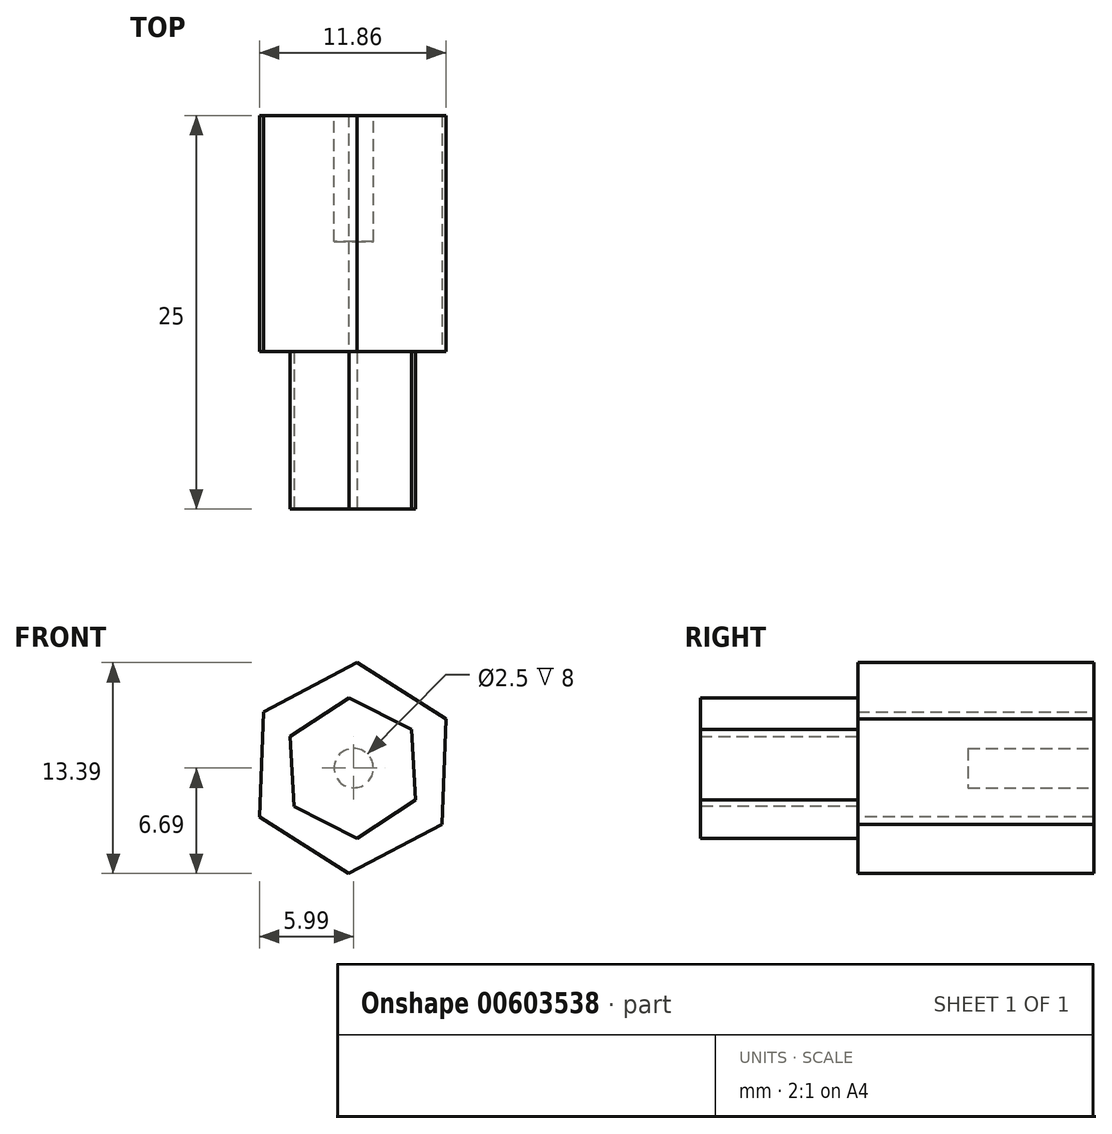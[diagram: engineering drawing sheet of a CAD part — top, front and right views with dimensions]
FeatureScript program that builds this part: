
annotation { "Feature Type Name" : "Feature", "Feature Type Description" : "" }
export const myFeature = defineFeature(function(context is Context, id is Id, definition is map)
    precondition{}
    {
        {
            var Q0;
            Q0=qCreatedBy(makeId("Front.planeOp"),FACE);
            var sketch = newSketch(context, id + "F0", { "sketchPlane" : qUnion([Q0])});
            skCircle(sketch, "E0", {"center": v(0, 0) * mm, "radius": 6.75 * mm, "construction": true});
            skCircle(sketch, "E1", {"center": v(0, 0) * mm, "radius": 4.5 * mm, "construction": true});
            skLineSegment(sketch, "E2", {"start": v(-5.99, -3.12) * mm, "end": v(-5.72, 3.58) * mm});
            skLineSegment(sketch, "E3.1.0", {"start": v(-0.32, -6.7) * mm, "end": v(-5.99, -3.12) * mm});
            skLineSegment(sketch, "E3.2.0", {"start": v(5.6, -3.57) * mm, "end": v(-0.32, -6.7) * mm});
            skLineSegment(sketch, "E3.3.0", {"start": v(5.87, 3.12) * mm, "end": v(5.6, -3.57) * mm});
            skLineSegment(sketch, "E3.4.0", {"start": v(0.2, 6.7) * mm, "end": v(5.87, 3.12) * mm});
            skLineSegment(sketch, "E3.5.0", {"start": v(-5.72, 3.58) * mm, "end": v(0.2, 6.7) * mm});
            skPoint(sketch, "E3.center", {"position": v(-0.06, 0) * mm});
            skLineSegment(sketch, "E4", {"start": v(-5.72, 3.58) * mm, "end": v(0, 0) * mm, "construction": true});
            skLineSegment(sketch, "E5", {"start": v(-5.99, -3.12) * mm, "end": v(0, 0) * mm, "construction": true});
            skLineSegment(sketch, "E6", {"start": v(-3.82, 2.39) * mm, "end": v(-4, -2.08) * mm});
            skLineSegment(sketch, "E7.1.0", {"start": v(-4, -2.08) * mm, "end": v(-0.21, -4.46) * mm});
            skLineSegment(sketch, "E7.2.0", {"start": v(-0.21, -4.46) * mm, "end": v(3.74, -2.38) * mm});
            skLineSegment(sketch, "E7.3.0", {"start": v(3.74, -2.38) * mm, "end": v(3.92, 2.08) * mm});
            skLineSegment(sketch, "E7.4.0", {"start": v(3.92, 2.08) * mm, "end": v(0.14, 4.47) * mm});
            skLineSegment(sketch, "E7.5.0", {"start": v(0.14, 4.47) * mm, "end": v(-3.81, 2.39) * mm});
            skPoint(sketch, "E7.center", {"position": v(-0.04, 0) * mm});
            skCircle(sketch, "E8", {"center": v(-15.66, -1.83) * mm, "radius": 4.5 * mm, "construction": true});
            skPoint(sketch, "E9.center", {"position": v(-15.72, -1.82) * mm});
            skLineSegment(sketch, "E10", {"start": v(-19.47, 0.56) * mm, "end": v(-19.65, -3.9) * mm});
            skLineSegment(sketch, "E11.1.0", {"start": v(-19.65, -3.9) * mm, "end": v(-15.87, -6.3) * mm});
            skLineSegment(sketch, "E11.2.0", {"start": v(-15.87, -6.3) * mm, "end": v(-11.92, -4.21) * mm});
            skLineSegment(sketch, "E11.3.0", {"start": v(-11.91, -4.2) * mm, "end": v(-11.74, 0.25) * mm});
            skLineSegment(sketch, "E11.4.0", {"start": v(-11.74, 0.26) * mm, "end": v(-15.52, 2.64) * mm});
            skLineSegment(sketch, "E11.5.0", {"start": v(-15.52, 2.64) * mm, "end": v(-19.47, 0.56) * mm});
            skPoint(sketch, "E11.center", {"position": v(-15.7, -1.83) * mm});
            skSolve(sketch);
        }
        {
            var Q0;
            Q0=makeQuery(id+"F0.imprint","IMPRINT",FACE,{"disambiguationData":[TD([[makeQuery(id+"F0.imprint","IMPRINT",EDGE,{"derivedFrom":sQuery(id+"F0.wireOp",EDGE,"E2")}),-1.0]])]});
            extrude(context, id + "F1", {"entities" : qUnion([Q0]), "depth" : 15 * mm, "offsetDistance" : 25 * mm});
        }
        {
            var Q0;
            Q0=makeQuery(id+"F1.opExtrude","CAP_FACE",FACE,{"disambiguationData":[OSD([sQuery(id+"F0.wireOp",EDGE,"E2"),sQuery(id+"F0.wireOp",EDGE,"E3.1.0"),sQuery(id+"F0.wireOp",EDGE,"E3.2.0"),sQuery(id+"F0.wireOp",EDGE,"E3.3.0"),sQuery(id+"F0.wireOp",EDGE,"E3.4.0"),sQuery(id+"F0.wireOp",EDGE,"E3.5.0")])],"isStart":false});
            var sketch = newSketch(context, id + "F2", { "sketchPlane" : qUnion([Q0])});
            skCircle(sketch, "E12", {"center": v(0, 0) * mm, "radius": 4.5 * mm, "construction": true});
            skLineSegment(sketch, "E13", {"start": v(-3.78, -2.45) * mm, "end": v(-4.03, 2) * mm});
            skLineSegment(sketch, "E14.1.0", {"start": v(0.2, -4.46) * mm, "end": v(-3.78, -2.45) * mm});
            skLineSegment(sketch, "E14.2.0", {"start": v(3.94, -2.01) * mm, "end": v(0.2, -4.46) * mm});
            skLineSegment(sketch, "E14.3.0", {"start": v(3.68, 2.44) * mm, "end": v(3.94, -2.01) * mm});
            skLineSegment(sketch, "E14.4.0", {"start": v(-0.3, 4.45) * mm, "end": v(3.68, 2.44) * mm});
            skLineSegment(sketch, "E14.5.0", {"start": v(-4.03, 2) * mm, "end": v(-0.3, 4.45) * mm});
            skPoint(sketch, "E14.center", {"position": v(-0.05, 0) * mm});
            skSolve(sketch);
        }
        {
            var Q0;
            Q0 = qSketchRegion(id + "F2", true);
            extrude(context, id + "F3", {"entities" : qUnion([Q0]), "operationType" : NewBodyOperationType.ADD, "depth" : 10 * mm, "offsetDistance" : 25 * mm});
        }
        {
            var Q0;
            Q0=makeQuery(id+"F1.opExtrude","CAP_FACE",FACE,{"disambiguationData":[OSD([sQuery(id+"F0.wireOp",EDGE,"E2"),sQuery(id+"F0.wireOp",EDGE,"E3.1.0"),sQuery(id+"F0.wireOp",EDGE,"E3.2.0"),sQuery(id+"F0.wireOp",EDGE,"E3.3.0"),sQuery(id+"F0.wireOp",EDGE,"E3.4.0"),sQuery(id+"F0.wireOp",EDGE,"E3.5.0")])],"isStart":true});
            var sketch = newSketch(context, id + "F4", { "sketchPlane" : qUnion([Q0])});
            skCircle(sketch, "E15", {"center": v(0, 0) * mm, "radius": 1.25 * mm});
            skSolve(sketch);
        }
        {
            var Q0;
            Q0 = qSketchRegion(id + "F4", true);
            extrude(context, id + "F5", {"entities" : qUnion([Q0]), "operationType" : NewBodyOperationType.REMOVE, "oppositeDirection" : true, "depth" : 8 * mm, "offsetDistance" : 25 * mm});
        }
    });
